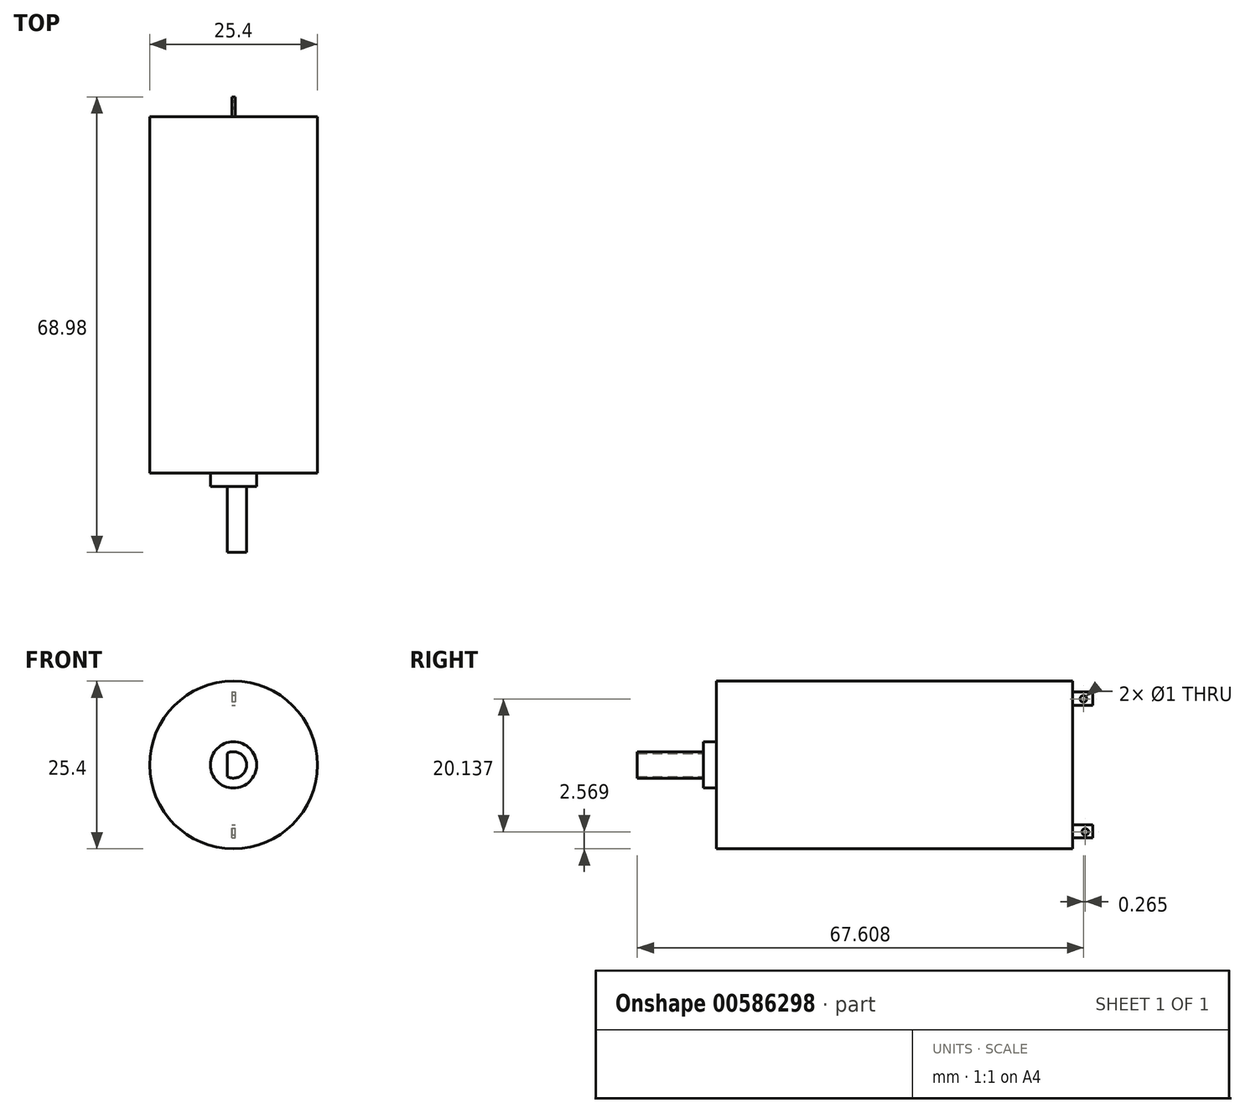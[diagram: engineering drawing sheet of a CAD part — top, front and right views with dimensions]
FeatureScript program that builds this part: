
annotation { "Feature Type Name" : "Feature", "Feature Type Description" : "" }
export const myFeature = defineFeature(function(context is Context, id is Id, definition is map)
    precondition{}
    {
        {
            var Q0;
            Q0=qCreatedBy(makeId("Front.planeOp"),FACE);
            var sketch = newSketch(context, id + "F0", { "sketchPlane" : qUnion([Q0])});
            skCircle(sketch, "E0", {"center": v(0, 0) * mm, "radius": 12.7 * mm});
            skSolve(sketch);
        }
        {
            var Q0;
            Q0=makeQuery(id+"F0.imprint","IMPRINT",FACE,{"disambiguationData":[TD([[makeQuery(id+"F0.imprint","IMPRINT",EDGE,{"derivedFrom":sQuery(id+"F0.wireOp",EDGE,"E0")}),1.0]])]});
            extrude(context, id + "F1", {"entities" : qUnion([Q0]), "depth" : 53.97 * mm, "offsetDistance" : 25.4 * mm});
        }
        {
            var Q0;
            Q0=makeQuery(id+"F1.opExtrude","CAP_FACE",FACE,{"disambiguationData":[OSD([sQuery(id+"F0.wireOp",EDGE,"E0")])],"isStart":false});
            var sketch = newSketch(context, id + "F2", { "sketchPlane" : qUnion([Q0])});
            skCircle(sketch, "E1", {"center": v(0, 0) * mm, "radius": 3.5 * mm});
            skSolve(sketch);
        }
        {
            var Q0;
            Q0=makeQuery(id+"F2.imprint","IMPRINT",FACE,{"disambiguationData":[TD([[makeQuery(id+"F2.imprint","IMPRINT",EDGE,{"derivedFrom":sQuery(id+"F2.wireOp",EDGE,"E1")}),1.0]])]});
            extrude(context, id + "F3", {"entities" : qUnion([Q0]), "operationType" : NewBodyOperationType.ADD, "depth" : 2 * mm, "offsetDistance" : 25.4 * mm});
        }
        {
            var Q0;
            Q0=makeQuery(id+"F3.opExtrude","CAP_FACE",FACE,{"disambiguationData":[OSD([sQuery(id+"F2.wireOp",EDGE,"E1")])],"isStart":false});
            var sketch = newSketch(context, id + "F4", { "sketchPlane" : qUnion([Q0])});
            skArc(sketch, "E2", {"start": v(-0.96, -1.75) * mm, "mid": v(2, 0) * mm, "end": v(-0.96, 1.75) * mm});
            skLineSegment(sketch, "E3", {"start": v(-0.96, 1.75) * mm, "end": v(-0.96, -1.75) * mm});
            skSolve(sketch);
        }
        {
            var Q0;
            Q0=makeQuery(id+"F4.imprint","IMPRINT",FACE,{"disambiguationData":[TD([[makeQuery(id+"F4.imprint","IMPRINT",EDGE,{"derivedFrom":sQuery(id+"F4.wireOp",EDGE,"E2")}),1.0]])]});
            extrude(context, id + "F5", {"entities" : qUnion([Q0]), "operationType" : NewBodyOperationType.ADD, "depth" : 10 * mm, "offsetDistance" : 25.4 * mm});
        }
        {
            var Q0;
            Q0=makeQuery(id+"F1.opExtrude","CAP_FACE",FACE,{"disambiguationData":[OSD([sQuery(id+"F0.wireOp",EDGE,"E0")])],"isStart":true});
            var sketch = newSketch(context, id + "F6", { "sketchPlane" : qUnion([Q0])});
            skLineSegment(sketch, "E4.bottom", {"start": v(0.25, 11.06) * mm, "end": v(-0.25, 11.06) * mm});
            skLineSegment(sketch, "E4.top", {"start": v(0.25, 9.06) * mm, "end": v(-0.25, 9.06) * mm});
            skLineSegment(sketch, "E4.left", {"start": v(0.25, 11.06) * mm, "end": v(0.25, 9.06) * mm});
            skLineSegment(sketch, "E4.right", {"start": v(-0.25, 11.06) * mm, "end": v(-0.25, 9.06) * mm});
            skLineSegment(sketch, "E5", {"start": v(3.29, 0) * mm, "end": v(-4.73, 0) * mm});
            skLineSegment(sketch, "E6.MirrorCS", {"start": v(0.25, -9.06) * mm, "end": v(-0.25, -9.06) * mm});
            skLineSegment(sketch, "E7.MirrorCS", {"start": v(0.25, -11.06) * mm, "end": v(0.25, -9.06) * mm});
            skLineSegment(sketch, "E8.MirrorCS", {"start": v(0.25, -11.06) * mm, "end": v(-0.25, -11.06) * mm});
            skLineSegment(sketch, "E9.MirrorCS", {"start": v(-0.25, -11.06) * mm, "end": v(-0.25, -9.06) * mm});
            skSolve(sketch);
        }
        {
            var Q0;
            Q0=makeQuery(id+"F6.imprint","IMPRINT",FACE,{"disambiguationData":[TD([[makeQuery(id+"F6.imprint","IMPRINT",EDGE,{"derivedFrom":sQuery(id+"F6.wireOp",EDGE,"E4.bottom")}),1.0]])]});
            var Q1;
            Q1=makeQuery(id+"F6.imprint","IMPRINT",FACE,{"disambiguationData":[TD([[makeQuery(id+"F6.imprint","IMPRINT",EDGE,{"derivedFrom":sQuery(id+"F6.wireOp",EDGE,"E6.MirrorCS")}),1.0]])]});
            extrude(context, id + "F7", {"entities" : qUnion([Q0, Q1]), "operationType" : NewBodyOperationType.ADD, "depth" : 3 * mm, "offsetDistance" : 25.4 * mm});
        }
        {
            var Q0;
            Q0=makeQuery(id+"F7.opExtrude","SWEPT_FACE",FACE,{"disambiguationData":[OSD([sQuery(id+"F6.wireOp",EDGE,"E7.MirrorCS")])]});
            var sketch = newSketch(context, id + "F8", { "sketchPlane" : qUnion([Q0])});
            skCircle(sketch, "E10", {"center": v(-1.9, -10.13) * mm, "radius": 0.5 * mm});
            skCircle(sketch, "E11", {"center": v(-1.63, 10) * mm, "radius": 0.5 * mm});
            skSolve(sketch);
        }
        {
            var Q0;
            Q0=makeQuery(id+"F8.imprint","IMPRINT",FACE,{"disambiguationData":[TD([[makeQuery(id+"F8.imprint","IMPRINT",EDGE,{"derivedFrom":sQuery(id+"F8.wireOp",EDGE,"E11")}),1.0]])]});
            var Q1;
            Q1=makeQuery(id+"F8.imprint","IMPRINT",FACE,{"disambiguationData":[TD([[makeQuery(id+"F8.imprint","IMPRINT",EDGE,{"derivedFrom":sQuery(id+"F8.wireOp",EDGE,"E10")}),1.0]])]});
            extrude(context, id + "F9", {"entities" : qUnion([Q0, Q1]), "operationType" : NewBodyOperationType.REMOVE, "oppositeDirection" : true, "depth" : 25.4 * mm, "offsetDistance" : 25.4 * mm});
        }
    });
